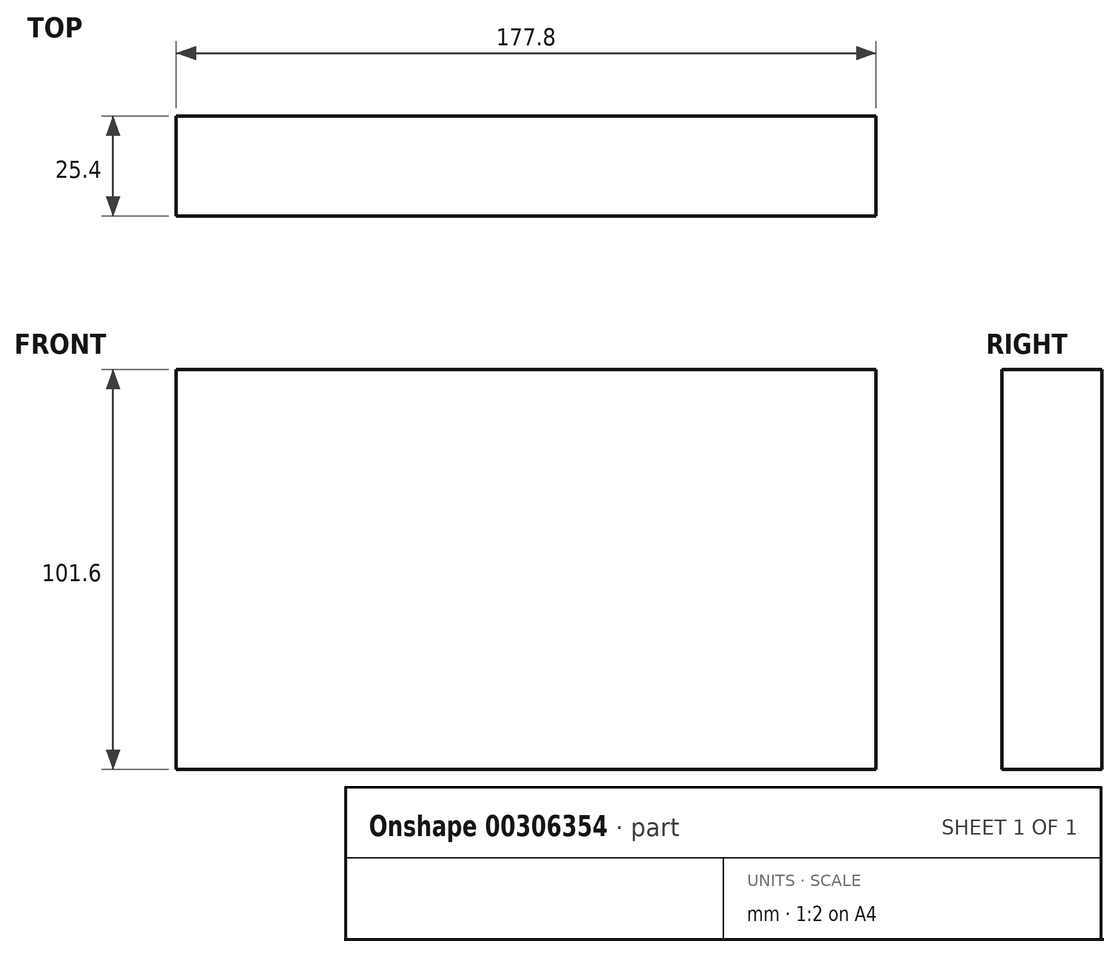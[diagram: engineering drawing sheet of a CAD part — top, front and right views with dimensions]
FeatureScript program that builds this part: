
annotation { "Feature Type Name" : "Feature", "Feature Type Description" : "" }
export const myFeature = defineFeature(function(context is Context, id is Id, definition is map)
    precondition{}
    {
        {
            var Q0;
            Q0=qCreatedBy(makeId("Front.planeOp"),FACE);
            var sketch = newSketch(context, id + "F0", { "sketchPlane" : qUnion([Q0])});
            skLineSegment(sketch, "E0.bottom", {"start": v(88.9, 50.8) * mm, "end": v(-88.9, 50.8) * mm});
            skLineSegment(sketch, "E0.top", {"start": v(88.9, -50.8) * mm, "end": v(-88.9, -50.8) * mm});
            skLineSegment(sketch, "E0.left", {"start": v(88.9, 50.8) * mm, "end": v(88.9, -50.8) * mm});
            skLineSegment(sketch, "E0.right", {"start": v(-88.9, 50.8) * mm, "end": v(-88.9, -50.8) * mm});
            skPoint(sketch, "E0.middle", {"position": v(0, 0) * mm});
            skSolve(sketch);
        }
        {
            var Q0;
            Q0=makeQuery(id+"F0.imprint","IMPRINT",FACE,{"disambiguationData":[TD([[makeQuery(id+"F0.imprint","IMPRINT",EDGE,{"derivedFrom":sQuery(id+"F0.wireOp",EDGE,"E0.bottom")}),1.0]])]});
            extrude(context, id + "F1", {"entities" : qUnion([Q0]), "depth" : 25.4 * mm});
        }
    });
